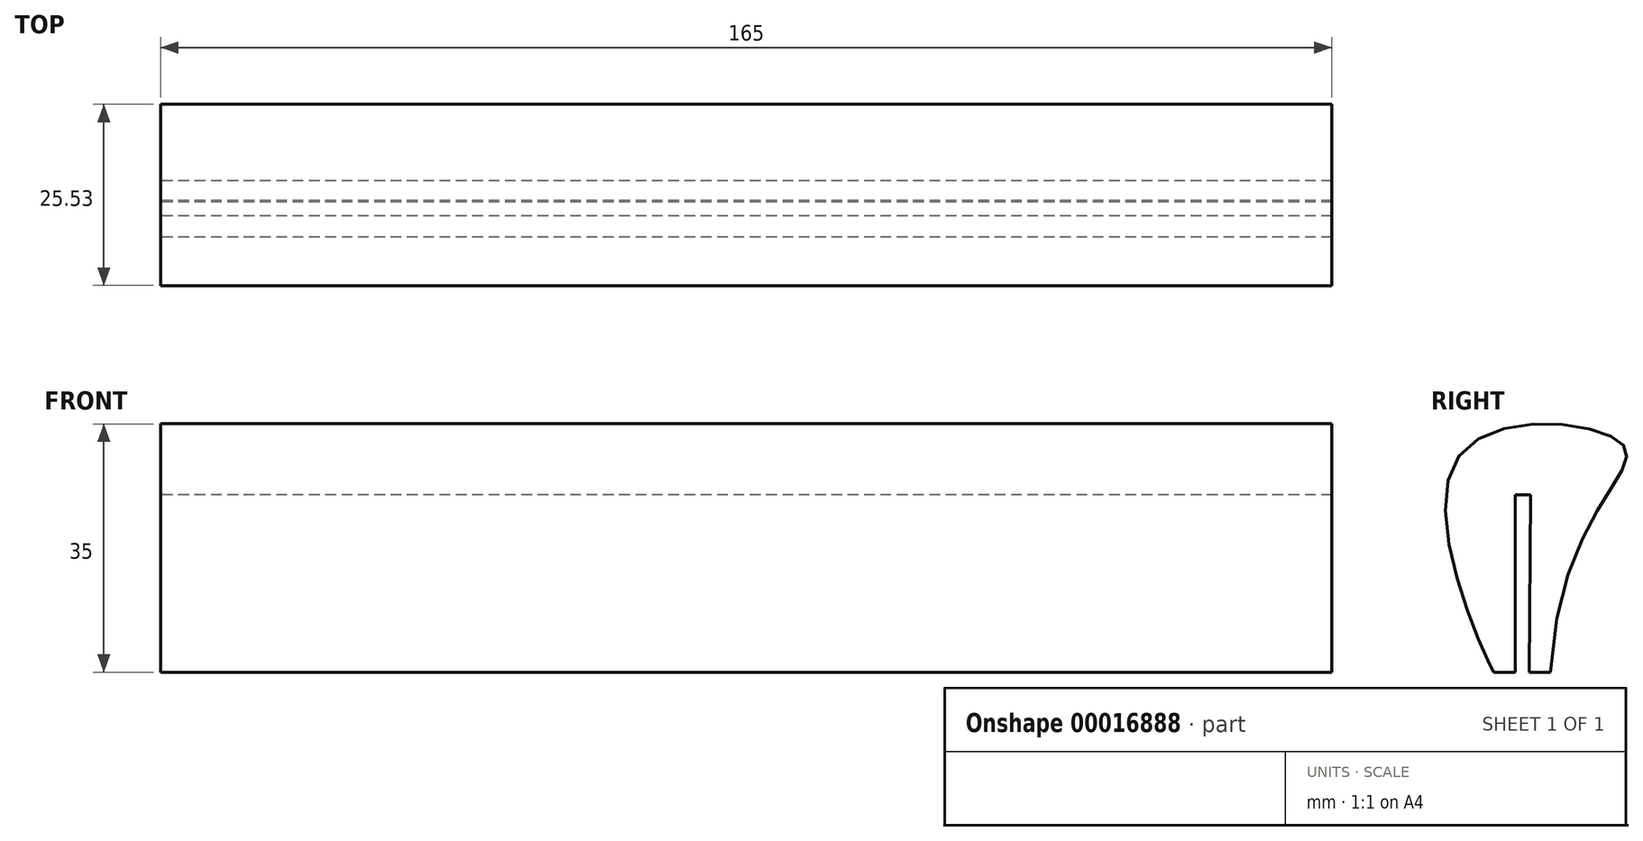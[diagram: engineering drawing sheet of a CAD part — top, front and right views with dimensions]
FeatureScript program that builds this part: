
annotation { "Feature Type Name" : "Feature", "Feature Type Description" : "" }
export const myFeature = defineFeature(function(context is Context, id is Id, definition is map)
    precondition{}
    {
        {
            var Q0;
            Q0=qCreatedBy(makeId("Right.planeOp"),FACE);
            var sketch = newSketch(context, id + "F0", { "sketchPlane" : qUnion([Q0])});
            skLineSegment(sketch, "E0", {"start": v(0, 0) * mm, "end": v(3, 0) * mm});
            skFitSpline(sketch, "E1", {"points": [v(3, 0) * mm, v(12.93, 32.34) * mm, v(-10.21, 30.03) * mm, v(-5, 0) * mm], "startDerivative": vector(8.7, 189.56) * mm, "endDerivative": vector(12.66, -21.17) * mm});
            skLineSegment(sketch, "E2", {"start": v(-5, 0) * mm, "end": v(-2, 0) * mm});
            skLineSegment(sketch, "E3", {"start": v(-2, 0) * mm, "end": v(-2, 25) * mm});
            skLineSegment(sketch, "E4", {"start": v(-2, 25) * mm, "end": v(0.2, 25) * mm});
            skLineSegment(sketch, "E5", {"start": v(0.2, 25) * mm, "end": v(0, 0) * mm});
            skSolve(sketch);
        }
        {
            var Q0;
            Q0 = qSketchRegion(id + "F0", true);
            extrude(context, id + "F1", {"entities" : qUnion([Q0]), "depth" : 165 * mm});
        }
    });
